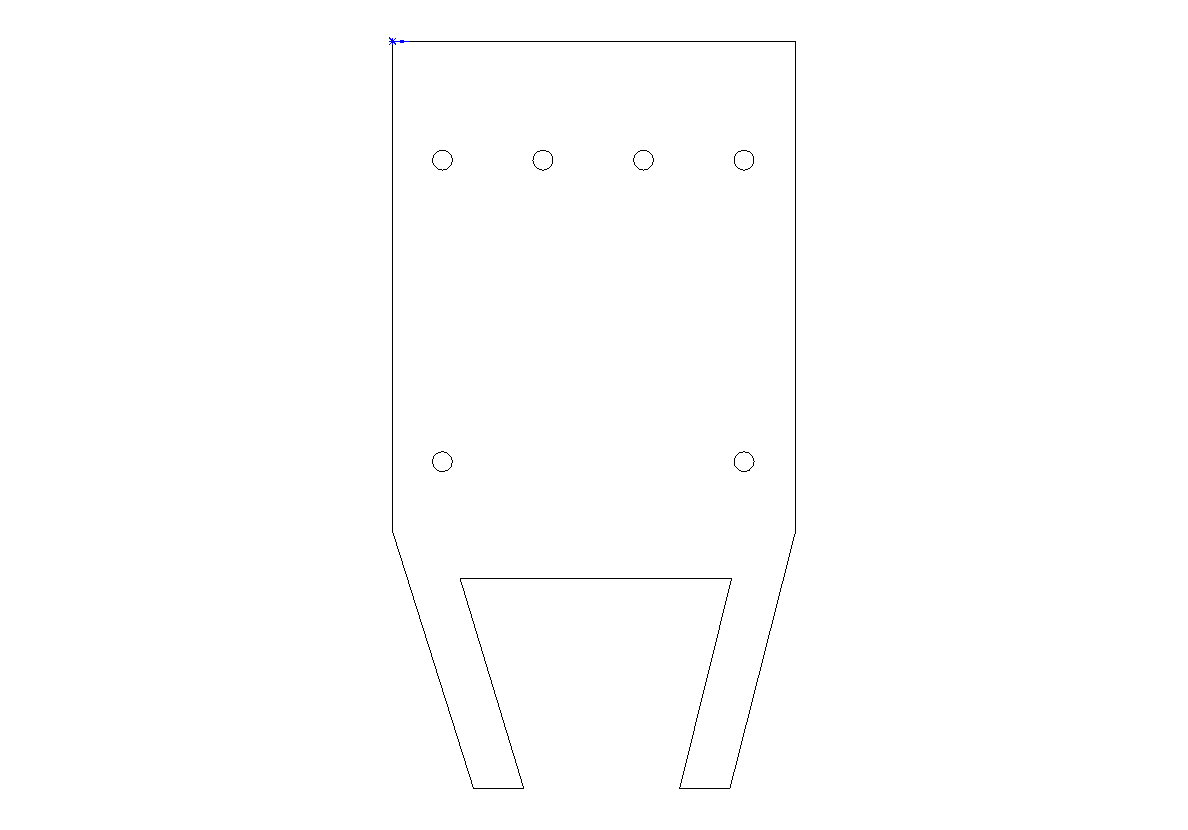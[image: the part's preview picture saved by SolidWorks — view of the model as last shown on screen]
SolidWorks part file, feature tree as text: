
SOLIDWORKS PART (.sldprt)
format: sldprt  version: not decoded by parser v0  size: 118,784 bytes
history: native  units: mm
features: sketch x3, extrude x3, material x1, pattern_linear x1 (+13 scaffold rows collapsed)
feature tree (21):
  scaffold x13  (default folders/planes/origin — collapsed)
  material  "Material <not specified>"
  sketch  "HFBR Base"  dims[D1=10.2mm D2=12.3444mm]
  extrude  "Extrude1"  Depth=7.62mm
  sketch  "Sketch2"  dims[c1.D1=6.477mm c1.D2=1.27mm c1.D3=1.27mm c1.D4=1.27mm c1.D5=6.5278mm c2.D4=6.5278mm c3.D4=~1.242818deg c4.D4=1.27mm c4.D6=1.27mm]
  extrude  "Extrude2"  Depth=7.62mm
  sketch  "Sketch3"  dims[D1=0.508mm D2=1.27mm D3=2.9972mm]
  extrude  "Pins"  Depth=3.81mm
  pattern_linear  "LPattern1"  Count1=4 Count2=2 Spacing1=2.54mm Spacing2=7.62mm
decode coverage: 7 of 7 modeling features carry decoded parameters
note: ~ marks probable driven/reference dimensions
note: suppression state not decoded; provenance and decode notes live in map.json
